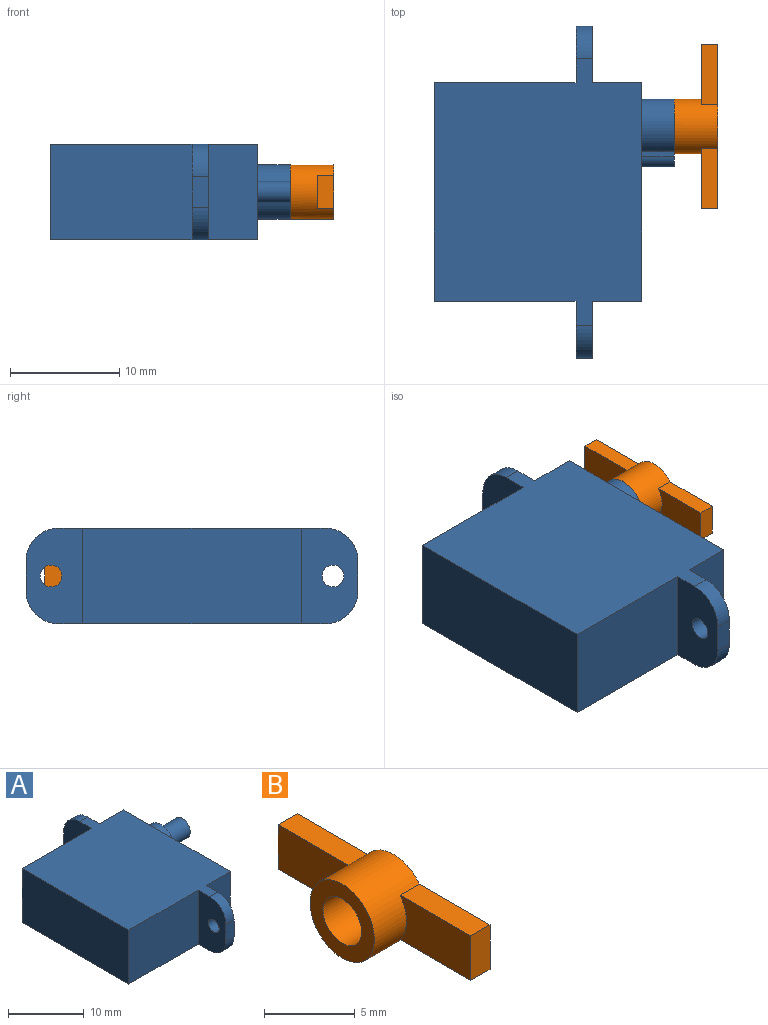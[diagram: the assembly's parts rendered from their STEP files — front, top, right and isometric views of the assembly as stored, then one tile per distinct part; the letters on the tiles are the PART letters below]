
ASSEMBLY  parts=2 mates=1
PART A: 27 faces, bbox 26x30.4x8.8 mm
  f0: plane 13x8.75mm, normal (0,-1,0), area 113.8mm2, adj f2,f6,f7,f13
  f1: plane 13x8.75mm, normal (0,1,0), area 113.8mm2, adj f2,f6,f7,f11
  f2: plane 20x8.75mm, normal (-1,0,0), area 175mm2, adj f0,f1,f6,f7
  f3: plane 8.75x4.5mm, normal (0,-1,0), area 39.4mm2, adj f4,f6,f7,f12
  f4: plane 20x8.75mm, normal (1,0,0), area 153.3mm2, adj f3,f5,f6,f7,f16,f17,f18,f19
  f5: plane 8.75x4.5mm, normal (0,1,0), area 39.4mm2, adj f4,f6,f7,f10
  f6: plane 24.39x19mm, normal (0,0,1), area 386.6mm2, adj f0,f1,f2,f3,f4,f5,f10,f11
  f7: plane 24.39x19mm, normal (0,0,-1), area 386.6mm2, adj f0,f1,f2,f3,f4,f5,f10,f11
  f8: cylinder r=1mm len=2mm, axis (-1,0,0), area 9.4mm2, adj f10,f11
  f9: plane 2.75x1.5mm, normal (0,1,0), area 4.1mm2, adj f10,f11,f23,f24
  f10: plane 8.75x5.2mm, normal (1,0,0), area 38.5mm2, adj f5,f6,f7,f8,f9,f23,f24
  f11: plane 8.75x5.2mm, normal (-1,0,0), area 38.5mm2, adj f1,f6,f7,f8,f9,f23,f24
  f12: plane 8.75x5.2mm, normal (1,0,0), area 38.5mm2, adj f3,f6,f7,f14,f15,f25,f26
  f13: plane 8.75x5.2mm, normal (-1,0,0), area 38.5mm2, adj f0,f6,f7,f14,f15,f25,f26
  f14: cylinder r=1mm len=2mm, axis (-1,0,0), area 9.4mm2, adj f12,f13
  f15: plane 2.75x1.5mm, normal (0,-1,0), area 4.1mm2, adj f12,f13,f25,f26
  f16: cylinder r=2.5mm len=5mm, axis (-1,0,0), area 41mm2, adj f4,f17,f19,f20
  f17: plane 3x0.41mm, normal (0,0,1), area 1.2mm2, adj f4,f16,f18,f20
  f18: cylinder r=0.99mm len=3mm, axis (-1,0,0), area 9.3mm2, adj f4,f17,f19,f20
  f19: plane 3x0.41mm, normal (0,0,-1), area 1.2mm2, adj f4,f16,f18,f20
  f20: plane 6.2x5mm, normal (1,0,0), area 14.6mm2, adj f16,f17,f18,f19,f21
  f21: cylinder r=1.5mm len=4mm, axis (-1,0,0), area 37.7mm2, adj f20,f22
  f22: plane 3x3mm, normal (1,0,0), area 7.1mm2, adj f21
  f23: cylinder r=3mm len=3mm, axis (1,0,0), area 7.1mm2, adj f7,f9,f10,f11
  f24: cylinder r=3mm len=3mm, axis (-1,0,0), area 7.1mm2, adj f6,f9,f10,f11
  f25: cylinder r=3mm len=3mm, axis (1,0,0), area 7.1mm2, adj f6,f12,f13,f15
  f26: cylinder r=3mm len=3mm, axis (-1,0,0), area 7.1mm2, adj f7,f12,f13,f15
PART B: 12 faces, bbox 4x15x5 mm
  f0: cylinder r=2.5mm len=5mm, axis (-1,0,0), area 53.2mm2, adj f1,f2,f4,f5,f6,f7,f8,f9
  f1: plane 15x5mm, normal (1,0,0), area 43.5mm2, adj f0,f3,f5,f6,f8,f9,f10,f11
  f2: plane 5x5mm, normal (-1,0,0), area 12.6mm2, adj f0,f11
  f3: plane 3x1.5mm, normal (0,-1,0), area 4.5mm2, adj f1,f4,f5,f6
  f4: plane 5.5x3mm, normal (-1,0,0), area 15.5mm2, adj f0,f3,f5,f6
  f5: plane 5.5x1.5mm, normal (0,0,1), area 8.2mm2, adj f0,f1,f3,f4
  f6: plane 5.5x1.5mm, normal (0,0,-1), area 8.2mm2, adj f0,f1,f3,f4
  f7: plane 5.5x3mm, normal (-1,0,0), area 15.5mm2, adj f0,f8,f9,f10
  f8: plane 5.5x1.5mm, normal (0,0,-1), area 8.2mm2, adj f0,f1,f7,f10
  f9: plane 5.5x1.5mm, normal (0,0,1), area 8.2mm2, adj f0,f1,f7,f10
  f10: plane 3x1.5mm, normal (0,1,0), area 4.5mm2, adj f1,f7,f8,f9
  f11: cylinder r=1.5mm len=4mm, axis (1,0,0), area 37.7mm2, adj f1,f2
PLACE A at identity fixed
PLACE B t=(3,6,0)mm
MATE fastened B.f0 <-> A.f16  axis (1,0,0) through (7,6,0)mm
